# Revit family: Window-Awning-Marvin-Clad_Contemporary
name_source: partatom
category: Windows
revit_build: Autodesk Revit 2018 (Build: 20170223_1515(x64)
units: mm (PartAtom-declared; Revit-internal decimal feet)

## family parameters
Always vertical = Yes
Cut with Voids When Loaded = No
Host = Wall
OmniClass Number = 23.30.20.17.21.14
OmniClass Title = Casement Windows
Room Calculation Point = No
Shared = No

## types (240) — shared parameters
Bottom Rail Standard = Yes
Bottom Rail Tall = No
Cladding Material = Aluminum-Marvin-Bronze
Default Head Height = 8' - 0"
Frame = Aluminum Clad
Glass Type = IG Low E II with Argon
Glazing Material = Glass-Marvin-IG Low E II with Argon
Interior Material = Wood-Marvin-Pine
Jamb Extension Visibility = Yes
Label Visibility = No
Lite Cut HV Grid = Yes
Lite Cut Prairie 9 = No
Lite Cut Prairie 9 Constraint = No
Lites High = 2
Lites High Constraint = 2
Lites Wide = 4
Manufacturer = Marvin Windows and Doors
Muntins Exterior Material = Aluminum-Marvin-Bronze
Muntins Exterior Visibility = Yes
Muntins Interior Material = Wood-Marvin-Pine
Muntins Interior Visibility = Yes
Offset = 0' - 2 29/32"
Prairie Corner Height = 0' - 4"
Prairie Corner Width = 0' - 4"
URL = www.marvin.com
Wall Closure = By host
Window Type = Clad Contemporary Awning

## per-type parameters (varying)
| type | DLO Height | DLO Width | Daylight Area | Description | Design Pressure | Height | Lites Wide Constraint | Nominal Height | Nominal Width | Rough Height | Rough Width | VO Height | VO Width | Vent Area | Width |
| CCNTPRYAWN1614 | 0' - 7 5/16" | 0' - 10 3/16" | 0.52 SF | 1614 AWNG | DP50 | 1' - 1 1/8" | 2 | 1' - 2" | 1' - 4" | 1' - 1 5/8" | 1' - 5" | 0' - 8" | 0' - 6 13/32" | 0.36 SF | 1' - 4" |
| CCNTPRYAWN1616 | 0' - 9 5/16" | 0' - 10 3/16" | 0.66 SF | 1616 AWNG | DP50 | 1' - 3 1/8" | 2 | 1' - 4" | 1' - 4" | 1' - 3 5/8" | 1' - 5" | 0' - 10" | 0' - 6 13/32" | 0.45 SF | 1' - 4" |
| CCNTPRYAWN1618 | 0' - 11 5/16" | 0' - 10 3/16" | 0.8 SF | 1618 AWNG | DP50 | 1' - 5 1/8" | 2 | 1' - 6" | 1' - 4" | 1' - 5 5/8" | 1' - 5" | 1' - 0" | 0' - 6 13/32" | 0.53 SF | 1' - 4" |
| CCNTPRYAWN1620 | 1' - 1 5/16" | 0' - 10 3/16" | 0.94 SF | 1620 AWNG | DP50 | 1' - 7 1/8" | 2 | 1' - 8" | 1' - 4" | 1' - 7 5/8" | 1' - 5" | 1' - 2" | 0' - 6 13/32" | 0.62 SF | 1' - 4" |
| CCNTPRYAWN1624 | 1' - 5 5/16" | 0' - 10 3/16" | 1.22 SF | 1624 AWNG | DP50 | 1' - 11 1/8" | 2 | 2' - 0" | 1' - 4" | 1' - 11 5/8" | 1' - 5" | 1' - 6" | 0' - 6 13/32" | 0.8 SF | 1' - 4" |
| CCNTPRYAWN1628 | 1' - 9 5/16" | 0' - 10 3/16" | 1.51 SF | 1628 AWNG | DP50 | 2' - 3 1/8" | 2 | 2' - 4" | 1' - 4" | 2' - 3 5/8" | 1' - 5" | 1' - 10" | 0' - 6 13/32" | 0.98 SF | 1' - 4" |
| CCNTPRYAWN1632 | 2' - 1 5/16" | 0' - 10 3/16" | 1.79 SF | 1632 AWNG | DP50 | 2' - 7 1/8" | 2 | 2' - 8" | 1' - 4" | 2' - 7 5/8" | 1' - 5" | 2' - 2" | 0' - 6 13/32" | 1.16 SF | 1' - 4" |
| CCNTPRYAWN1636 | 2' - 5 5/16" | 0' - 10 3/16" | 2.07 SF | 1636 AWNG | DP50 | 2' - 11 1/8" | 2 | 3' - 0" | 1' - 4" | 2' - 11 5/8" | 1' - 5" | 2' - 6" | 0' - 6 13/32" | 1.34 SF | 1' - 4" |
| CCNTPRYAWN1640 | 2' - 9 5/16" | 0' - 10 3/16" | 2.36 SF | 1640 AWNG | DP50 | 3' - 3 1/8" | 2 | 3' - 4" | 1' - 4" | 3' - 3 5/8" | 1' - 5" | 2' - 10" | 0' - 6 13/32" | 1.51 SF | 1' - 4" |
| CCNTPRYAWN1644 | 3' - 1 5/16" | 0' - 10 3/16" | 2.64 SF | 1644 AWNG | DP50 | 3' - 7 1/8" | 2 | 3' - 8" | 1' - 4" | 3' - 7 5/8" | 1' - 5" | 3' - 2" | 0' - 6 13/32" | 1.69 SF | 1' - 4" |
| CCNTPRYAWN1648 | 3' - 5 5/16" | 0' - 10 3/16" | 2.92 SF | 1648 AWNG | DP50 | 3' - 11 1/8" | 2 | 4' - 0" | 1' - 4" | 3' - 11 5/8" | 1' - 5" | 3' - 6" | 0' - 6 13/32" | 1.87 SF | 1' - 4" |
| CCNTPRYAWN1654 | 3' - 11 5/16" | 0' - 10 3/16" | 3.35 SF | 1654 AWNG | DP50 | 4' - 5 1/8" | 2 | 4' - 6" | 1' - 4" | 4' - 5 5/8" | 1' - 5" | 4' - 0" | 0' - 6 13/32" | 2.14 SF | 1' - 4" |
| CCNTPRYAWN1656 | 4' - 1 5/16" | 0' - 10 3/16" | 3.49 SF | 1656 AWNG | DP50 | 4' - 7 1/8" | 2 | 4' - 8" | 1' - 4" | 4' - 7 5/8" | 1' - 5" | 4' - 2" | 0' - 6 13/32" | 2.22 SF | 1' - 4" |
| CCNTPRYAWN1660 | 4' - 5 5/16" | 0' - 10 3/16" | 3.77 SF | 1660 AWNG | DP50 | 4' - 11 1/8" | 2 | 5' - 0" | 1' - 4" | 4' - 11 5/8" | 1' - 5" | 4' - 6" | 0' - 6 13/32" | 2.4 SF | 1' - 4" |
| CCNTPRYAWN1664 | 4' - 9 5/16" | 0' - 10 3/16" | 4.05 SF | 1664 AWNG | DP50 | 5' - 3 1/8" | 2 | 5' - 4" | 1' - 4" | 5' - 3 5/8" | 1' - 5" | 4' - 10" | 0' - 6 13/32" | 2.58 SF | 1' - 4" |
| CCNTPRYAWN1672 | 5' - 5 5/16" | 0' - 10 3/16" | 4.62 SF | 1672 AWNG | DP50 | 5' - 11 1/8" | 2 | 6' - 0" | 1' - 4" | 5' - 11 5/8" | 1' - 5" | 5' - 6" | 0' - 6 13/32" | 2.94 SF | 1' - 4" |
| CCNTPRYAWN1814 | 0' - 7 5/16" | 1' - 0 3/16" | 0.62 SF | 1814 AWNG | DP50 | 1' - 1 1/8" | 4 | 1' - 2" | 1' - 6" | 1' - 1 5/8" | 1' - 7" | 0' - 8" | 0' - 8 13/32" | 0.47 SF | 1' - 6" |
| CCNTPRYAWN1816 | 0' - 9 5/16" | 1' - 0 3/16" | 0.79 SF | 1816 AWNG | DP50 | 1' - 3 1/8" | 4 | 1' - 4" | 1' - 6" | 1' - 3 5/8" | 1' - 7" | 0' - 10" | 0' - 8 13/32" | 0.58 SF | 1' - 6" |
| CCNTPRYAWN1818 | 0' - 11 5/16" | 1' - 0 3/16" | 0.96 SF | 1818 AWNG | DP50 | 1' - 5 1/8" | 4 | 1' - 6" | 1' - 6" | 1' - 5 5/8" | 1' - 7" | 1' - 0" | 0' - 8 13/32" | 0.7 SF | 1' - 6" |
| CCNTPRYAWN1820 | 1' - 1 5/16" | 1' - 0 3/16" | 1.13 SF | 1820 AWNG | DP50 | 1' - 7 1/8" | 4 | 1' - 8" | 1' - 6" | 1' - 7 5/8" | 1' - 7" | 1' - 2" | 0' - 8 13/32" | 0.82 SF | 1' - 6" |
| CCNTPRYAWN1824 | 1' - 5 5/16" | 1' - 0 3/16" | 1.47 SF | 1824 AWNG | DP50 | 1' - 11 1/8" | 4 | 2' - 0" | 1' - 6" | 1' - 11 5/8" | 1' - 7" | 1' - 6" | 0' - 8 13/32" | 1.05 SF | 1' - 6" |
| CCNTPRYAWN1828 | 1' - 9 5/16" | 1' - 0 3/16" | 1.8 SF | 1828 AWNG | DP50 | 2' - 3 1/8" | 4 | 2' - 4" | 1' - 6" | 2' - 3 5/8" | 1' - 7" | 1' - 10" | 0' - 8 13/32" | 1.28 SF | 1' - 6" |
| CCNTPRYAWN1832 | 2' - 1 5/16" | 1' - 0 3/16" | 2.14 SF | 1832 AWNG | DP50 | 2' - 7 1/8" | 4 | 2' - 8" | 1' - 6" | 2' - 7 5/8" | 1' - 7" | 2' - 2" | 0' - 8 13/32" | 1.52 SF | 1' - 6" |
| CCNTPRYAWN1836 | 2' - 5 5/16" | 1' - 0 3/16" | 2.48 SF | 1836 AWNG | DP50 | 2' - 11 1/8" | 4 | 3' - 0" | 1' - 6" | 2' - 11 5/8" | 1' - 7" | 2' - 6" | 0' - 8 13/32" | 1.75 SF | 1' - 6" |
| CCNTPRYAWN1840 | 2' - 9 5/16" | 1' - 0 3/16" | 2.82 SF | 1840 AWNG | DP50 | 3' - 3 1/8" | 4 | 3' - 4" | 1' - 6" | 3' - 3 5/8" | 1' - 7" | 2' - 10" | 0' - 8 13/32" | 1.99 SF | 1' - 6" |
| CCNTPRYAWN1844 | 3' - 1 5/16" | 1' - 0 3/16" | 3.16 SF | 1844 AWNG | DP50 | 3' - 7 1/8" | 4 | 3' - 8" | 1' - 6" | 3' - 7 5/8" | 1' - 7" | 3' - 2" | 0' - 8 13/32" | 2.22 SF | 1' - 6" |
| CCNTPRYAWN1848 | 3' - 5 5/16" | 1' - 0 3/16" | 3.5 SF | 1848 AWNG | DP50 | 3' - 11 1/8" | 4 | 4' - 0" | 1' - 6" | 3' - 11 5/8" | 1' - 7" | 3' - 6" | 0' - 8 13/32" | 2.45 SF | 1' - 6" |
| CCNTPRYAWN1854 | 3' - 11 5/16" | 1' - 0 3/16" | 4 SF | 1854 AWNG | DP50 | 4' - 5 1/8" | 4 | 4' - 6" | 1' - 6" | 4' - 5 5/8" | 1' - 7" | 4' - 0" | 0' - 8 13/32" | 2.8 SF | 1' - 6" |
| CCNTPRYAWN1856 | 4' - 1 5/16" | 1' - 0 3/16" | 4.17 SF | 1856 AWNG | DP50 | 4' - 7 1/8" | 4 | 4' - 8" | 1' - 6" | 4' - 7 5/8" | 1' - 7" | 4' - 2" | 0' - 8 13/32" | 2.92 SF | 1' - 6" |
| CCNTPRYAWN1860 | 4' - 5 5/16" | 1' - 0 3/16" | 4.51 SF | 1860 AWNG | DP50 | 4' - 11 1/8" | 4 | 5' - 0" | 1' - 6" | 4' - 11 5/8" | 1' - 7" | 4' - 6" | 0' - 8 13/32" | 3.15 SF | 1' - 6" |
| CCNTPRYAWN1864 | 4' - 9 5/16" | 1' - 0 3/16" | 4.85 SF | 1864 AWNG | DP50 | 5' - 3 1/8" | 4 | 5' - 4" | 1' - 6" | 5' - 3 5/8" | 1' - 7" | 4' - 10" | 0' - 8 13/32" | 3.39 SF | 1' - 6" |
| CCNTPRYAWN1872 | 5' - 5 5/16" | 1' - 0 3/16" | 5.53 SF | 1872 AWNG | DP50 | 5' - 11 1/8" | 4 | 6' - 0" | 1' - 6" | 5' - 11 5/8" | 1' - 7" | 5' - 6" | 0' - 8 13/32" | 3.85 SF | 1' - 6" |
| CCNTPRYAWN2014 | 0' - 7 5/16" | 1' - 2 3/16" | 0.72 SF | 2014 AWNG | DP50 | 1' - 1 1/8" | 4 | 1' - 2" | 1' - 8" | 1' - 1 5/8" | 1' - 9" | 0' - 8" | 1' - 0 29/32" | 0.72 SF | 1' - 8" |
| CCNTPRYAWN2016 | 0' - 9 5/16" | 1' - 2 3/16" | 0.92 SF | 2016 AWNG | DP50 | 1' - 3 1/8" | 4 | 1' - 4" | 1' - 8" | 1' - 3 5/8" | 1' - 9" | 0' - 10" | 1' - 0 29/32" | 0.9 SF | 1' - 8" |
| CCNTPRYAWN2018 | 0' - 11 5/16" | 1' - 2 3/16" | 1.11 SF | 2018 AWNG | DP50 | 1' - 5 1/8" | 4 | 1' - 6" | 1' - 8" | 1' - 5 5/8" | 1' - 9" | 1' - 0" | 1' - 0 29/32" | 1.08 SF | 1' - 8" |
| CCNTPRYAWN2020 | 1' - 1 5/16" | 1' - 2 3/16" | 1.31 SF | 2020 AWNG | DP50 | 1' - 7 1/8" | 4 | 1' - 8" | 1' - 8" | 1' - 7 5/8" | 1' - 9" | 1' - 2" | 1' - 0 29/32" | 1.25 SF | 1' - 8" |
| CCNTPRYAWN2024 | 1' - 5 5/16" | 1' - 2 3/16" | 1.71 SF | 2024 AWNG | DP50 | 1' - 11 1/8" | 4 | 2' - 0" | 1' - 8" | 1' - 11 5/8" | 1' - 9" | 1' - 6" | 1' - 0 29/32" | 1.61 SF | 1' - 8" |
| CCNTPRYAWN2028 | 1' - 9 5/16" | 1' - 2 3/16" | 2.1 SF | 2028 AWNG | DP50 | 2' - 3 1/8" | 4 | 2' - 4" | 1' - 8" | 2' - 3 5/8" | 1' - 9" | 1' - 10" | 1' - 0 29/32" | 1.97 SF | 1' - 8" |
| CCNTPRYAWN2032 | 2' - 1 5/16" | 1' - 2 3/16" | 2.49 SF | 2032 AWNG | DP50 | 2' - 7 1/8" | 4 | 2' - 8" | 1' - 8" | 2' - 7 5/8" | 1' - 9" | 2' - 2" | 1' - 0 29/32" | 2.33 SF | 1' - 8" |
| CCNTPRYAWN2036 | 2' - 5 5/16" | 1' - 2 3/16" | 2.89 SF | 2036 AWNG | DP50 | 2' - 11 1/8" | 4 | 3' - 0" | 1' - 8" | 2' - 11 5/8" | 1' - 9" | 2' - 6" | 1' - 0 29/32" | 2.69 SF | 1' - 8" |
| CCNTPRYAWN2040 | 2' - 9 5/16" | 1' - 2 3/16" | 3.28 SF | 2040 AWNG | DP50 | 3' - 3 1/8" | 4 | 3' - 4" | 1' - 8" | 3' - 3 5/8" | 1' - 9" | 2' - 10" | 1' - 0 29/32" | 3.04 SF | 1' - 8" |
| CCNTPRYAWN2044 | 3' - 1 5/16" | 1' - 2 3/16" | 3.68 SF | 2044 AWNG | DP50 | 3' - 7 1/8" | 4 | 3' - 8" | 1' - 8" | 3' - 7 5/8" | 1' - 9" | 3' - 2" | 1' - 0 29/32" | 3.4 SF | 1' - 8" |
| CCNTPRYAWN2048 | 3' - 5 5/16" | 1' - 2 3/16" | 4.07 SF | 2048 AWNG | DP50 | 3' - 11 1/8" | 4 | 4' - 0" | 1' - 8" | 3' - 11 5/8" | 1' - 9" | 3' - 6" | 1' - 0 29/32" | 3.76 SF | 1' - 8" |
| CCNTPRYAWN2054 | 3' - 11 5/16" | 1' - 2 3/16" | 4.66 SF | 2054 AWNG | DP50 | 4' - 5 1/8" | 4 | 4' - 6" | 1' - 8" | 4' - 5 5/8" | 1' - 9" | 4' - 0" | 1' - 0 29/32" | 4.3 SF | 1' - 8" |
| CCNTPRYAWN2056 | 4' - 1 5/16" | 1' - 2 3/16" | 4.86 SF | 2056 AWNG | DP50 | 4' - 7 1/8" | 4 | 4' - 8" | 1' - 8" | 4' - 7 5/8" | 1' - 9" | 4' - 2" | 1' - 0 29/32" | 4.48 SF | 1' - 8" |
| CCNTPRYAWN2060 | 4' - 5 5/16" | 1' - 2 3/16" | 5.25 SF | 2060 AWNG | DP50 | 4' - 11 1/8" | 4 | 5' - 0" | 1' - 8" | 4' - 11 5/8" | 1' - 9" | 4' - 6" | 1' - 0 29/32" | 4.84 SF | 1' - 8" |
| CCNTPRYAWN2064 | 4' - 9 5/16" | 1' - 2 3/16" | 5.65 SF | 2064 AWNG | DP50 | 5' - 3 1/8" | 4 | 5' - 4" | 1' - 8" | 5' - 3 5/8" | 1' - 9" | 4' - 10" | 1' - 0 29/32" | 5.19 SF | 1' - 8" |
| CCNTPRYAWN2072 | 5' - 5 5/16" | 1' - 2 3/16" | 6.43 SF | 2072 AWNG | DP50 | 5' - 11 1/8" | 4 | 6' - 0" | 1' - 8" | 5' - 11 5/8" | 1' - 9" | 5' - 6" | 1' - 0 29/32" | 5.91 SF | 1' - 8" |
| CCNTPRYAWN2414 | 0' - 7 5/16" | 1' - 6 3/16" | 0.92 SF | 2414 AWNG | DP50 | 1' - 1 1/8" | 4 | 1' - 2" | 2' - 0" | 1' - 1 5/8" | 2' - 1" | 0' - 8" | 1' - 4 29/32" | 0.94 SF | 2' - 0" |
| CCNTPRYAWN2416 | 0' - 9 5/16" | 1' - 6 3/16" | 1.18 SF | 2416 AWNG | DP50 | 1' - 3 1/8" | 4 | 1' - 4" | 2' - 0" | 1' - 3 5/8" | 2' - 1" | 0' - 10" | 1' - 4 29/32" | 1.17 SF | 2' - 0" |
| CCNTPRYAWN2418 | 0' - 11 5/16" | 1' - 6 3/16" | 1.43 SF | 2418 AWNG | DP50 | 1' - 5 1/8" | 4 | 1' - 6" | 2' - 0" | 1' - 5 5/8" | 2' - 1" | 1' - 0" | 1' - 4 29/32" | 1.41 SF | 2' - 0" |
| CCNTPRYAWN2420 | 1' - 1 5/16" | 1' - 6 3/16" | 1.68 SF | 2420 AWNG | DP50 | 1' - 7 1/8" | 4 | 1' - 8" | 2' - 0" | 1' - 7 5/8" | 2' - 1" | 1' - 2" | 1' - 4 29/32" | 1.64 SF | 2' - 0" |
| CCNTPRYAWN2424 | 1' - 5 5/16" | 1' - 6 3/16" | 2.19 SF | 2424 AWNG | DP50 | 1' - 11 1/8" | 4 | 2' - 0" | 2' - 0" | 1' - 11 5/8" | 2' - 1" | 1' - 6" | 1' - 4 29/32" | 2.11 SF | 2' - 0" |
| CCNTPRYAWN2428 | 1' - 9 5/16" | 1' - 6 3/16" | 2.69 SF | 2428 AWNG | DP50 | 2' - 3 1/8" | 4 | 2' - 4" | 2' - 0" | 2' - 3 5/8" | 2' - 1" | 1' - 10" | 1' - 4 29/32" | 2.58 SF | 2' - 0" |
| CCNTPRYAWN2432 | 2' - 1 5/16" | 1' - 6 3/16" | 3.2 SF | 2432 AWNG | DP50 | 2' - 7 1/8" | 4 | 2' - 8" | 2' - 0" | 2' - 7 5/8" | 2' - 1" | 2' - 2" | 1' - 4 29/32" | 3.05 SF | 2' - 0" |
| CCNTPRYAWN2436 | 2' - 5 5/16" | 1' - 6 3/16" | 3.7 SF | 2436 AWNG | DP50 | 2' - 11 1/8" | 4 | 3' - 0" | 2' - 0" | 2' - 11 5/8" | 2' - 1" | 2' - 6" | 1' - 4 29/32" | 3.52 SF | 2' - 0" |
| CCNTPRYAWN2440 | 2' - 9 5/16" | 1' - 6 3/16" | 4.21 SF | 2440 AWNG | DP50 | 3' - 3 1/8" | 4 | 3' - 4" | 2' - 0" | 3' - 3 5/8" | 2' - 1" | 2' - 10" | 1' - 4 29/32" | 3.99 SF | 2' - 0" |
| CCNTPRYAWN2444 | 3' - 1 5/16" | 1' - 6 3/16" | 4.71 SF | 2444 AWNG | DP50 | 3' - 7 1/8" | 4 | 3' - 8" | 2' - 0" | 3' - 7 5/8" | 2' - 1" | 3' - 2" | 1' - 4 29/32" | 4.46 SF | 2' - 0" |
| CCNTPRYAWN2448 | 3' - 5 5/16" | 1' - 6 3/16" | 5.22 SF | 2448 AWNG | DP50 | 3' - 11 1/8" | 4 | 4' - 0" | 2' - 0" | 3' - 11 5/8" | 2' - 1" | 3' - 6" | 1' - 4 29/32" | 4.93 SF | 2' - 0" |
| CCNTPRYAWN2454 | 3' - 11 5/16" | 1' - 6 3/16" | 5.98 SF | 2454 AWNG | DP50 | 4' - 5 1/8" | 4 | 4' - 6" | 2' - 0" | 4' - 5 5/8" | 2' - 1" | 4' - 0" | 1' - 4 29/32" | 5.63 SF | 2' - 0" |
| CCNTPRYAWN2456 | 4' - 1 5/16" | 1' - 6 3/16" | 6.23 SF | 2456 AWNG | DP50 | 4' - 7 1/8" | 4 | 4' - 8" | 2' - 0" | 4' - 7 5/8" | 2' - 1" | 4' - 2" | 1' - 4 29/32" | 5.87 SF | 2' - 0" |
| CCNTPRYAWN2460 | 4' - 5 5/16" | 1' - 6 3/16" | 6.73 SF | 2460 AWNG | DP50 | 4' - 11 1/8" | 4 | 5' - 0" | 2' - 0" | 4' - 11 5/8" | 2' - 1" | 4' - 6" | 1' - 4 29/32" | 6.34 SF | 2' - 0" |
| CCNTPRYAWN2464 | 4' - 9 5/16" | 1' - 6 3/16" | 7.24 SF | 2464 AWNG | DP50 | 5' - 3 1/8" | 4 | 5' - 4" | 2' - 0" | 5' - 3 5/8" | 2' - 1" | 4' - 10" | 1' - 4 29/32" | 6.8 SF | 2' - 0" |
| CCNTPRYAWN2472 | 5' - 5 5/16" | 1' - 6 3/16" | 8.25 SF | 2472 AWNG | DP50 | 5' - 11 1/8" | 4 | 6' - 0" | 2' - 0" | 5' - 11 5/8" | 2' - 1" | 5' - 6" | 1' - 4 29/32" | 7.74 SF | 2' - 0" |
| CCNTPRYAWN2614 | 0' - 7 5/16" | 1' - 8 3/16" | 1.03 SF | 2614 AWNG | DP50 | 1' - 1 1/8" | 4 | 1' - 2" | 2' - 2" | 1' - 1 5/8" | 2' - 3" | 0' - 8" | 1' - 6 29/32" | 1.05 SF | 2' - 2" |
| CCNTPRYAWN2616 | 0' - 9 5/16" | 1' - 8 3/16" | 1.31 SF | 2616 AWNG | DP50 | 1' - 3 1/8" | 4 | 1' - 4" | 2' - 2" | 1' - 3 5/8" | 2' - 3" | 0' - 10" | 1' - 6 29/32" | 1.31 SF | 2' - 2" |
| CCNTPRYAWN2618 | 0' - 11 5/16" | 1' - 8 3/16" | 1.59 SF | 2618 AWNG | DP50 | 1' - 5 1/8" | 4 | 1' - 6" | 2' - 2" | 1' - 5 5/8" | 2' - 3" | 1' - 0" | 1' - 6 29/32" | 1.58 SF | 2' - 2" |
| CCNTPRYAWN2620 | 1' - 1 5/16" | 1' - 8 3/16" | 1.87 SF | 2620 AWNG | DP50 | 1' - 7 1/8" | 4 | 1' - 8" | 2' - 2" | 1' - 7 5/8" | 2' - 3" | 1' - 2" | 1' - 6 29/32" | 1.84 SF | 2' - 2" |
| CCNTPRYAWN2624 | 1' - 5 5/16" | 1' - 8 3/16" | 2.43 SF | 2624 AWNG | DP50 | 1' - 11 1/8" | 4 | 2' - 0" | 2' - 2" | 1' - 11 5/8" | 2' - 3" | 1' - 6" | 1' - 6 29/32" | 2.36 SF | 2' - 2" |
| CCNTPRYAWN2628 | 1' - 9 5/16" | 1' - 8 3/16" | 2.99 SF | 2628 AWNG | DP50 | 2' - 3 1/8" | 4 | 2' - 4" | 2' - 2" | 2' - 3 5/8" | 2' - 3" | 1' - 10" | 1' - 6 29/32" | 2.89 SF | 2' - 2" |
| CCNTPRYAWN2632 | 2' - 1 5/16" | 1' - 8 3/16" | 3.55 SF | 2632 AWNG | DP50 | 2' - 7 1/8" | 4 | 2' - 8" | 2' - 2" | 2' - 7 5/8" | 2' - 3" | 2' - 2" | 1' - 6 29/32" | 3.41 SF | 2' - 2" |
| CCNTPRYAWN2636 | 2' - 5 5/16" | 1' - 8 3/16" | 4.11 SF | 2636 AWNG | DP50 | 2' - 11 1/8" | 4 | 3' - 0" | 2' - 2" | 2' - 11 5/8" | 2' - 3" | 2' - 6" | 1' - 6 29/32" | 3.94 SF | 2' - 2" |
| CCNTPRYAWN2640 | 2' - 9 5/16" | 1' - 8 3/16" | 4.67 SF | 2640 AWNG | DP50 | 3' - 3 1/8" | 4 | 3' - 4" | 2' - 2" | 3' - 3 5/8" | 2' - 3" | 2' - 10" | 1' - 6 29/32" | 4.46 SF | 2' - 2" |
| CCNTPRYAWN2644 | 3' - 1 5/16" | 1' - 8 3/16" | 5.23 SF | 2644 AWNG | DP50 | 3' - 7 1/8" | 4 | 3' - 8" | 2' - 2" | 3' - 7 5/8" | 2' - 3" | 3' - 2" | 1' - 6 29/32" | 4.99 SF | 2' - 2" |
| CCNTPRYAWN2648 | 3' - 5 5/16" | 1' - 8 3/16" | 5.79 SF | 2648 AWNG | DP50 | 3' - 11 1/8" | 4 | 4' - 0" | 2' - 2" | 3' - 11 5/8" | 2' - 3" | 3' - 6" | 1' - 6 29/32" | 5.51 SF | 2' - 2" |
| CCNTPRYAWN2654 | 3' - 11 5/16" | 1' - 8 3/16" | 6.63 SF | 2654 AWNG | DP50 | 4' - 5 1/8" | 4 | 4' - 6" | 2' - 2" | 4' - 5 5/8" | 2' - 3" | 4' - 0" | 1' - 6 29/32" | 6.3 SF | 2' - 2" |
| CCNTPRYAWN2656 | 4' - 1 5/16" | 1' - 8 3/16" | 6.91 SF | 2656 AWNG | DP50 | 4' - 7 1/8" | 4 | 4' - 8" | 2' - 2" | 4' - 7 5/8" | 2' - 3" | 4' - 2" | 1' - 6 29/32" | 6.56 SF | 2' - 2" |
| CCNTPRYAWN2660 | 4' - 5 5/16" | 1' - 8 3/16" | 7.47 SF | 2660 AWNG | DP50 | 4' - 11 1/8" | 4 | 5' - 0" | 2' - 2" | 4' - 11 5/8" | 2' - 3" | 4' - 6" | 1' - 6 29/32" | 7.09 SF | 2' - 2" |
| CCNTPRYAWN2664 | 4' - 9 5/16" | 1' - 8 3/16" | 8.03 SF | 2664 AWNG | DP50 | 5' - 3 1/8" | 4 | 5' - 4" | 2' - 2" | 5' - 3 5/8" | 2' - 3" | 4' - 10" | 1' - 6 29/32" | 7.61 SF | 2' - 2" |
| CCNTPRYAWN2672 | 5' - 5 5/16" | 1' - 8 3/16" | 9.16 SF | 2672 AWNG | DP50 | 5' - 11 1/8" | 4 | 6' - 0" | 2' - 2" | 5' - 11 5/8" | 2' - 3" | 5' - 6" | 1' - 6 29/32" | 8.66 SF | 2' - 2" |
| CCNTPRYAWN2814 | 0' - 7 5/16" | 1' - 10 3/16" | 1.13 SF | 2814 AWNG | DP50 | 1' - 1 1/8" | 4 | 1' - 2" | 2' - 4" | 1' - 1 5/8" | 2' - 5" | 0' - 8" | 1' - 8 29/32" | 1.16 SF | 2' - 4" |
| CCNTPRYAWN2816 | 0' - 9 5/16" | 1' - 10 3/16" | 1.43 SF | 2816 AWNG | DP50 | 1' - 3 1/8" | 4 | 1' - 4" | 2' - 4" | 1' - 3 5/8" | 2' - 5" | 0' - 10" | 1' - 8 29/32" | 1.45 SF | 2' - 4" |
| CCNTPRYAWN2818 | 0' - 11 5/16" | 1' - 10 3/16" | 1.74 SF | 2818 AWNG | DP50 | 1' - 5 1/8" | 4 | 1' - 6" | 2' - 4" | 1' - 5 5/8" | 2' - 5" | 1' - 0" | 1' - 8 29/32" | 1.74 SF | 2' - 4" |
| CCNTPRYAWN2820 | 1' - 1 5/16" | 1' - 10 3/16" | 2.05 SF | 2820 AWNG | DP50 | 1' - 7 1/8" | 4 | 1' - 8" | 2' - 4" | 1' - 7 5/8" | 2' - 5" | 1' - 2" | 1' - 8 29/32" | 2.03 SF | 2' - 4" |
| CCNTPRYAWN2824 | 1' - 5 5/16" | 1' - 10 3/16" | 2.67 SF | 2824 AWNG | DP50 | 1' - 11 1/8" | 4 | 2' - 0" | 2' - 4" | 1' - 11 5/8" | 2' - 5" | 1' - 6" | 1' - 8 29/32" | 2.61 SF | 2' - 4" |
| CCNTPRYAWN2828 | 1' - 9 5/16" | 1' - 10 3/16" | 3.28 SF | 2828 AWNG | DP50 | 2' - 3 1/8" | 4 | 2' - 4" | 2' - 4" | 2' - 3 5/8" | 2' - 5" | 1' - 10" | 1' - 8 29/32" | 3.19 SF | 2' - 4" |
| CCNTPRYAWN2832 | 2' - 1 5/16" | 1' - 10 3/16" | 3.9 SF | 2832 AWNG | DP50 | 2' - 7 1/8" | 4 | 2' - 8" | 2' - 4" | 2' - 7 5/8" | 2' - 5" | 2' - 2" | 1' - 8 29/32" | 3.77 SF | 2' - 4" |
| CCNTPRYAWN2836 | 2' - 5 5/16" | 1' - 10 3/16" | 4.52 SF | 2836 AWNG | DP50 | 2' - 11 1/8" | 4 | 3' - 0" | 2' - 4" | 2' - 11 5/8" | 2' - 5" | 2' - 6" | 1' - 8 29/32" | 4.35 SF | 2' - 4" |
| CCNTPRYAWN2840 | 2' - 9 5/16" | 1' - 10 3/16" | 5.13 SF | 2840 AWNG | DP50 | 3' - 3 1/8" | 4 | 3' - 4" | 2' - 4" | 3' - 3 5/8" | 2' - 5" | 2' - 10" | 1' - 8 29/32" | 4.93 SF | 2' - 4" |
| CCNTPRYAWN2844 | 3' - 1 5/16" | 1' - 10 3/16" | 5.75 SF | 2844 AWNG | DP50 | 3' - 7 1/8" | 4 | 3' - 8" | 2' - 4" | 3' - 7 5/8" | 2' - 5" | 3' - 2" | 1' - 8 29/32" | 5.51 SF | 2' - 4" |
| CCNTPRYAWN2848 | 3' - 5 5/16" | 1' - 10 3/16" | 6.37 SF | 2848 AWNG | DP50 | 3' - 11 1/8" | 4 | 4' - 0" | 2' - 4" | 3' - 11 5/8" | 2' - 5" | 3' - 6" | 1' - 8 29/32" | 6.09 SF | 2' - 4" |
| CCNTPRYAWN2854 | 3' - 11 5/16" | 1' - 10 3/16" | 7.29 SF | 2854 AWNG | DP50 | 4' - 5 1/8" | 4 | 4' - 6" | 2' - 4" | 4' - 5 5/8" | 2' - 5" | 4' - 0" | 1' - 8 29/32" | 6.97 SF | 2' - 4" |
| CCNTPRYAWN2856 | 4' - 1 5/16" | 1' - 10 3/16" | 7.6 SF | 2856 AWNG | DP50 | 4' - 7 1/8" | 4 | 4' - 8" | 2' - 4" | 4' - 7 5/8" | 2' - 5" | 4' - 2" | 1' - 8 29/32" | 7.26 SF | 2' - 4" |
| CCNTPRYAWN2860 | 4' - 5 5/16" | 1' - 10 3/16" | 8.21 SF | 2860 AWNG | DP50 | 4' - 11 1/8" | 4 | 5' - 0" | 2' - 4" | 4' - 11 5/8" | 2' - 5" | 4' - 6" | 1' - 8 29/32" | 7.84 SF | 2' - 4" |
| CCNTPRYAWN2864 | 4' - 9 5/16" | 1' - 10 3/16" | 8.83 SF | 2864 AWNG | DP50 | 5' - 3 1/8" | 4 | 5' - 4" | 2' - 4" | 5' - 3 5/8" | 2' - 5" | 4' - 10" | 1' - 8 29/32" | 8.42 SF | 2' - 4" |
| CCNTPRYAWN2872 | 5' - 5 5/16" | 1' - 10 3/16" | 10.06 SF | 2872 AWNG | DP50 | 5' - 11 1/8" | 4 | 6' - 0" | 2' - 4" | 5' - 11 5/8" | 2' - 5" | 5' - 6" | 1' - 8 29/32" | 9.58 SF | 2' - 4" |
| CCNTPRYAWN3014 | 0' - 7 5/16" | 2' - 0 3/16" | 1.23 SF | 3014 AWNG | DP50 | 1' - 1 1/8" | 4 | 1' - 2" | 2' - 6" | 1' - 1 5/8" | 2' - 7" | 0' - 8" | 1' - 10 29/32" | 1.27 SF | 2' - 6" |
| CCNTPRYAWN3016 | 0' - 9 5/16" | 2' - 0 3/16" | 1.56 SF | 3016 AWNG | DP50 | 1' - 3 1/8" | 4 | 1' - 4" | 2' - 6" | 1' - 3 5/8" | 2' - 7" | 0' - 10" | 1' - 10 29/32" | 1.59 SF | 2' - 6" |
| CCNTPRYAWN3018 | 0' - 11 5/16" | 2' - 0 3/16" | 1.9 SF | 3018 AWNG | DP50 | 1' - 5 1/8" | 4 | 1' - 6" | 2' - 6" | 1' - 5 5/8" | 2' - 7" | 1' - 0" | 1' - 10 29/32" | 1.91 SF | 2' - 6" |
| CCNTPRYAWN3020 | 1' - 1 5/16" | 2' - 0 3/16" | 2.24 SF | 3020 AWNG | DP50 | 1' - 7 1/8" | 4 | 1' - 8" | 2' - 6" | 1' - 7 5/8" | 2' - 7" | 1' - 2" | 1' - 10 29/32" | 2.23 SF | 2' - 6" |
| CCNTPRYAWN3024 | 1' - 5 5/16" | 2' - 0 3/16" | 2.91 SF | 3024 AWNG | DP50 | 1' - 11 1/8" | 4 | 2' - 0" | 2' - 6" | 1' - 11 5/8" | 2' - 7" | 1' - 6" | 1' - 10 29/32" | 2.86 SF | 2' - 6" |
| CCNTPRYAWN3028 | 1' - 9 5/16" | 2' - 0 3/16" | 3.58 SF | 3028 AWNG | DP50 | 2' - 3 1/8" | 4 | 2' - 4" | 2' - 6" | 2' - 3 5/8" | 2' - 7" | 1' - 10" | 1' - 10 29/32" | 3.5 SF | 2' - 6" |
| CCNTPRYAWN3032 | 2' - 1 5/16" | 2' - 0 3/16" | 4.25 SF | 3032 AWNG | DP50 | 2' - 7 1/8" | 4 | 2' - 8" | 2' - 6" | 2' - 7 5/8" | 2' - 7" | 2' - 2" | 1' - 10 29/32" | 4.13 SF | 2' - 6" |
| CCNTPRYAWN3036 | 2' - 5 5/16" | 2' - 0 3/16" | 4.92 SF | 3036 AWNG | DP50 | 2' - 11 1/8" | 4 | 3' - 0" | 2' - 6" | 2' - 11 5/8" | 2' - 7" | 2' - 6" | 1' - 10 29/32" | 4.77 SF | 2' - 6" |
| CCNTPRYAWN3040 | 2' - 9 5/16" | 2' - 0 3/16" | 5.6 SF | 3040 AWNG | DP50 | 3' - 3 1/8" | 4 | 3' - 4" | 2' - 6" | 3' - 3 5/8" | 2' - 7" | 2' - 10" | 1' - 10 29/32" | 5.41 SF | 2' - 6" |
| CCNTPRYAWN3044 | 3' - 1 5/16" | 2' - 0 3/16" | 6.27 SF | 3044 AWNG | DP50 | 3' - 7 1/8" | 4 | 3' - 8" | 2' - 6" | 3' - 7 5/8" | 2' - 7" | 3' - 2" | 1' - 10 29/32" | 6.04 SF | 2' - 6" |
| CCNTPRYAWN3048 | 3' - 5 5/16" | 2' - 0 3/16" | 6.94 SF | 3048 AWNG | DP50 | 3' - 11 1/8" | 4 | 4' - 0" | 2' - 6" | 3' - 11 5/8" | 2' - 7" | 3' - 6" | 1' - 10 29/32" | 6.68 SF | 2' - 6" |
| CCNTPRYAWN3054 | 3' - 11 5/16" | 2' - 0 3/16" | 7.95 SF | 3054 AWNG | DP50 | 4' - 5 1/8" | 4 | 4' - 6" | 2' - 6" | 4' - 5 5/8" | 2' - 7" | 4' - 0" | 1' - 10 29/32" | 7.63 SF | 2' - 6" |
| CCNTPRYAWN3056 | 4' - 1 5/16" | 2' - 0 3/16" | 8.28 SF | 3056 AWNG | DP50 | 4' - 7 1/8" | 4 | 4' - 8" | 2' - 6" | 4' - 7 5/8" | 2' - 7" | 4' - 2" | 1' - 10 29/32" | 7.95 SF | 2' - 6" |
| CCNTPRYAWN3060 | 4' - 5 5/16" | 2' - 0 3/16" | 8.95 SF | 3060 AWNG | DP50 | 4' - 11 1/8" | 4 | 5' - 0" | 2' - 6" | 4' - 11 5/8" | 2' - 7" | 4' - 6" | 1' - 10 29/32" | 8.59 SF | 2' - 6" |
| CCNTPRYAWN3064 | 4' - 9 5/16" | 2' - 0 3/16" | 9.63 SF | 3064 AWNG | DP50 | 5' - 3 1/8" | 4 | 5' - 4" | 2' - 6" | 5' - 3 5/8" | 2' - 7" | 4' - 10" | 1' - 10 29/32" | 9.22 SF | 2' - 6" |
| CCNTPRYAWN3072 | 5' - 5 5/16" | 2' - 0 3/16" | 10.97 SF | 3072 AWNG | DP50 | 5' - 11 1/8" | 4 | 6' - 0" | 2' - 6" | 5' - 11 5/8" | 2' - 7" | 5' - 6" | 1' - 10 29/32" | 10.49 SF | 2' - 6" |
| CCNTPRYAWN3214 | 0' - 7 5/16" | 2' - 2 3/16" | 1.33 SF | 3214 AWNG | DP50 | 1' - 1 1/8" | 4 | 1' - 2" | 2' - 8" | 1' - 1 5/8" | 2' - 9" | 0' - 8" | 2' - 0 29/32" | 1.38 SF | 2' - 8" |
| CCNTPRYAWN3216 | 0' - 9 5/16" | 2' - 2 3/16" | 1.69 SF | 3216 AWNG | DP50 | 1' - 3 1/8" | 4 | 1' - 4" | 2' - 8" | 1' - 3 5/8" | 2' - 9" | 0' - 10" | 2' - 0 29/32" | 1.73 SF | 2' - 8" |
| CCNTPRYAWN3218 | 0' - 11 5/16" | 2' - 2 3/16" | 2.06 SF | 3218 AWNG | DP50 | 1' - 5 1/8" | 4 | 1' - 6" | 2' - 8" | 1' - 5 5/8" | 2' - 9" | 1' - 0" | 2' - 0 29/32" | 2.08 SF | 2' - 8" |
| CCNTPRYAWN3220 | 1' - 1 5/16" | 2' - 2 3/16" | 2.42 SF | 3220 AWNG | DP50 | 1' - 7 1/8" | 4 | 1' - 8" | 2' - 8" | 1' - 7 5/8" | 2' - 9" | 1' - 2" | 2' - 0 29/32" | 2.42 SF | 2' - 8" |
| CCNTPRYAWN3224 | 1' - 5 5/16" | 2' - 2 3/16" | 3.15 SF | 3224 AWNG | DP50 | 1' - 11 1/8" | 4 | 2' - 0" | 2' - 8" | 1' - 11 5/8" | 2' - 9" | 1' - 6" | 2' - 0 29/32" | 3.11 SF | 2' - 8" |
| CCNTPRYAWN3228 | 1' - 9 5/16" | 2' - 2 3/16" | 3.88 SF | 3228 AWNG | DP50 | 2' - 3 1/8" | 4 | 2' - 4" | 2' - 8" | 2' - 3 5/8" | 2' - 9" | 1' - 10" | 2' - 0 29/32" | 3.8 SF | 2' - 8" |
| CCNTPRYAWN3232 | 2' - 1 5/16" | 2' - 2 3/16" | 4.6 SF | 3232 AWNG | DP50 | 2' - 7 1/8" | 4 | 2' - 8" | 2' - 8" | 2' - 7 5/8" | 2' - 9" | 2' - 2" | 2' - 0 29/32" | 4.5 SF | 2' - 8" |
| CCNTPRYAWN3236 | 2' - 5 5/16" | 2' - 2 3/16" | 5.33 SF | 3236 AWNG | DP50 | 2' - 11 1/8" | 4 | 3' - 0" | 2' - 8" | 2' - 11 5/8" | 2' - 9" | 2' - 6" | 2' - 0 29/32" | 5.19 SF | 2' - 8" |
| CCNTPRYAWN3240 | 2' - 9 5/16" | 2' - 2 3/16" | 6.06 SF | 3240 AWNG | DP50 | 3' - 3 1/8" | 4 | 3' - 4" | 2' - 8" | 3' - 3 5/8" | 2' - 9" | 2' - 10" | 2' - 0 29/32" | 5.88 SF | 2' - 8" |
| CCNTPRYAWN3244 | 3' - 1 5/16" | 2' - 2 3/16" | 6.79 SF | 3244 AWNG | DP50 | 3' - 7 1/8" | 4 | 3' - 8" | 2' - 8" | 3' - 7 5/8" | 2' - 9" | 3' - 2" | 2' - 0 29/32" | 6.57 SF | 2' - 8" |
| CCNTPRYAWN3248 | 3' - 5 5/16" | 2' - 2 3/16" | 7.51 SF | 3248 AWNG | DP50 | 3' - 11 1/8" | 4 | 4' - 0" | 2' - 8" | 3' - 11 5/8" | 2' - 9" | 3' - 6" | 2' - 0 29/32" | 7.26 SF | 2' - 8" |
| CCNTPRYAWN3254 | 3' - 11 5/16" | 2' - 2 3/16" | 8.6 SF | 3254 AWNG | DP50 | 4' - 5 1/8" | 4 | 4' - 6" | 2' - 8" | 4' - 5 5/8" | 2' - 9" | 4' - 0" | 2' - 0 29/32" | 8.3 SF | 2' - 8" |
| CCNTPRYAWN3256 | 4' - 1 5/16" | 2' - 2 3/16" | 8.97 SF | 3256 AWNG | DP50 | 4' - 7 1/8" | 4 | 4' - 8" | 2' - 8" | 4' - 7 5/8" | 2' - 9" | 4' - 2" | 2' - 0 29/32" | 8.64 SF | 2' - 8" |
| CCNTPRYAWN3260 | 4' - 5 5/16" | 2' - 2 3/16" | 9.7 SF | 3260 AWNG | DP50 | 4' - 11 1/8" | 4 | 5' - 0" | 2' - 8" | 4' - 11 5/8" | 2' - 9" | 4' - 6" | 2' - 0 29/32" | 9.34 SF | 2' - 8" |
| CCNTPRYAWN3264 | 4' - 9 5/16" | 2' - 2 3/16" | 10.42 SF | 3264 AWNG | DP50 | 5' - 3 1/8" | 4 | 5' - 4" | 2' - 8" | 5' - 3 5/8" | 2' - 9" | 4' - 10" | 2' - 0 29/32" | 10.03 SF | 2' - 8" |
| CCNTPRYAWN3272 | 5' - 5 5/16" | 2' - 2 3/16" | 11.88 SF | 3272 AWNG | DP50 | 5' - 11 1/8" | 4 | 6' - 0" | 2' - 8" | 5' - 11 5/8" | 2' - 9" | 5' - 6" | 2' - 0 29/32" | 11.41 SF | 2' - 8" |
| CCNTPRYAWN3614 | 0' - 7 5/16" | 2' - 6 3/16" | 1.53 SF | 3614 AWNG | DP50 | 1' - 1 1/8" | 4 | 1' - 2" | 3' - 0" | 1' - 1 5/8" | 3' - 1" | 0' - 8" | 2' - 4 29/32" | 1.61 SF | 3' - 0" |
| CCNTPRYAWN3616 | 0' - 9 5/16" | 2' - 6 3/16" | 1.95 SF | 3616 AWNG | DP50 | 1' - 3 1/8" | 4 | 1' - 4" | 3' - 0" | 1' - 3 5/8" | 3' - 1" | 0' - 10" | 2' - 4 29/32" | 2.01 SF | 3' - 0" |
| CCNTPRYAWN3618 | 0' - 11 5/16" | 2' - 6 3/16" | 2.37 SF | 3618 AWNG | DP50 | 1' - 5 1/8" | 4 | 1' - 6" | 3' - 0" | 1' - 5 5/8" | 3' - 1" | 1' - 0" | 2' - 4 29/32" | 2.41 SF | 3' - 0" |
| CCNTPRYAWN3620 | 1' - 1 5/16" | 2' - 6 3/16" | 2.79 SF | 3620 AWNG | DP50 | 1' - 7 1/8" | 4 | 1' - 8" | 3' - 0" | 1' - 7 5/8" | 3' - 1" | 1' - 2" | 2' - 4 29/32" | 2.81 SF | 3' - 0" |
| CCNTPRYAWN3624 | 1' - 5 5/16" | 2' - 6 3/16" | 3.63 SF | 3624 AWNG | DP50 | 1' - 11 1/8" | 4 | 2' - 0" | 3' - 0" | 1' - 11 5/8" | 3' - 1" | 1' - 6" | 2' - 4 29/32" | 3.61 SF | 3' - 0" |
| CCNTPRYAWN3628 | 1' - 9 5/16" | 2' - 6 3/16" | 4.47 SF | 3628 AWNG | DP50 | 2' - 3 1/8" | 4 | 2' - 4" | 3' - 0" | 2' - 3 5/8" | 3' - 1" | 1' - 10" | 2' - 4 29/32" | 4.42 SF | 3' - 0" |
| CCNTPRYAWN3632 | 2' - 1 5/16" | 2' - 6 3/16" | 5.31 SF | 3632 AWNG | DP50 | 2' - 7 1/8" | 4 | 2' - 8" | 3' - 0" | 2' - 7 5/8" | 3' - 1" | 2' - 2" | 2' - 4 29/32" | 5.22 SF | 3' - 0" |
| CCNTPRYAWN3636 | 2' - 5 5/16" | 2' - 6 3/16" | 6.14 SF | 3636 AWNG | DP50 | 2' - 11 1/8" | 4 | 3' - 0" | 3' - 0" | 2' - 11 5/8" | 3' - 1" | 2' - 6" | 2' - 4 29/32" | 6.02 SF | 3' - 0" |
| CCNTPRYAWN3640 | 2' - 9 5/16" | 2' - 6 3/16" | 6.98 SF | 3640 AWNG | DP50 | 3' - 3 1/8" | 4 | 3' - 4" | 3' - 0" | 3' - 3 5/8" | 3' - 1" | 2' - 10" | 2' - 4 29/32" | 6.82 SF | 3' - 0" |
| CCNTPRYAWN3644 | 3' - 1 5/16" | 2' - 6 3/16" | 7.82 SF | 3644 AWNG | DP50 | 3' - 7 1/8" | 4 | 3' - 8" | 3' - 0" | 3' - 7 5/8" | 3' - 1" | 3' - 2" | 2' - 4 29/32" | 7.63 SF | 3' - 0" |
| CCNTPRYAWN3648 | 3' - 5 5/16" | 2' - 6 3/16" | 8.66 SF | 3648 AWNG | DP50 | 3' - 11 1/8" | 4 | 4' - 0" | 3' - 0" | 3' - 11 5/8" | 3' - 1" | 3' - 6" | 2' - 4 29/32" | 8.43 SF | 3' - 0" |
| CCNTPRYAWN3654 | 3' - 11 5/16" | 2' - 6 3/16" | 9.92 SF | 3654 AWNG | DP50 | 4' - 5 1/8" | 4 | 4' - 6" | 3' - 0" | 4' - 5 5/8" | 3' - 1" | 4' - 0" | 2' - 4 29/32" | 9.63 SF | 3' - 0" |
| CCNTPRYAWN3656 | 4' - 1 5/16" | 2' - 6 3/16" | 10.34 SF | 3656 AWNG | DP50 | 4' - 7 1/8" | 4 | 4' - 8" | 3' - 0" | 4' - 7 5/8" | 3' - 1" | 4' - 2" | 2' - 4 29/32" | 10.03 SF | 3' - 0" |
| CCNTPRYAWN3660 | 4' - 5 5/16" | 2' - 6 3/16" | 11.18 SF | 3660 AWNG | DP50 | 4' - 11 1/8" | 4 | 5' - 0" | 3' - 0" | 4' - 11 5/8" | 3' - 1" | 4' - 6" | 2' - 4 29/32" | 10.84 SF | 3' - 0" |
| CCNTPRYAWN3664 | 4' - 9 5/16" | 2' - 6 3/16" | 12.01 SF | 3664 AWNG | DP50 | 5' - 3 1/8" | 4 | 5' - 4" | 3' - 0" | 5' - 3 5/8" | 3' - 1" | 4' - 10" | 2' - 4 29/32" | 11.64 SF | 3' - 0" |
| CCNTPRYAWN3672 | 5' - 5 5/16" | 2' - 6 3/16" | 13.69 SF | 3672 AWNG | DP50 | 5' - 11 1/8" | 4 | 6' - 0" | 3' - 0" | 5' - 11 5/8" | 3' - 1" | 5' - 6" | 2' - 4 29/32" | 13.24 SF | 3' - 0" |
| CCNTPRYAWN4014 | 0' - 7 5/16" | 2' - 10 3/16" | 1.74 SF | 4014 AWNG | DP50 | 1' - 1 1/8" | 4 | 1' - 2" | 3' - 4" | 1' - 1 5/8" | 3' - 5" | 0' - 8" | 2' - 8 29/32" | 1.83 SF | 3' - 4" |
| CCNTPRYAWN4016 | 0' - 9 5/16" | 2' - 10 3/16" | 2.21 SF | 4016 AWNG | DP50 | 1' - 3 1/8" | 4 | 1' - 4" | 3' - 4" | 1' - 3 5/8" | 3' - 5" | 0' - 10" | 2' - 8 29/32" | 2.29 SF | 3' - 4" |
| CCNTPRYAWN4018 | 0' - 11 5/16" | 2' - 10 3/16" | 2.69 SF | 4018 AWNG | DP50 | 1' - 5 1/8" | 4 | 1' - 6" | 3' - 4" | 1' - 5 5/8" | 3' - 5" | 1' - 0" | 2' - 8 29/32" | 2.74 SF | 3' - 4" |
| CCNTPRYAWN4020 | 1' - 1 5/16" | 2' - 10 3/16" | 3.16 SF | 4020 AWNG | DP50 | 1' - 7 1/8" | 4 | 1' - 8" | 3' - 4" | 1' - 7 5/8" | 3' - 5" | 1' - 2" | 2' - 8 29/32" | 3.2 SF | 3' - 4" |
| CCNTPRYAWN4024 | 1' - 5 5/16" | 2' - 10 3/16" | 4.11 SF | 4024 AWNG | DP50 | 1' - 11 1/8" | 4 | 2' - 0" | 3' - 4" | 1' - 11 5/8" | 3' - 5" | 1' - 6" | 2' - 8 29/32" | 4.11 SF | 3' - 4" |
| CCNTPRYAWN4028 | 1' - 9 5/16" | 2' - 10 3/16" | 5.06 SF | 4028 AWNG | DP50 | 2' - 3 1/8" | 4 | 2' - 4" | 3' - 4" | 2' - 3 5/8" | 3' - 5" | 1' - 10" | 2' - 8 29/32" | 5.03 SF | 3' - 4" |
| CCNTPRYAWN4032 | 2' - 1 5/16" | 2' - 10 3/16" | 6.01 SF | 4032 AWNG | DP50 | 2' - 7 1/8" | 4 | 2' - 8" | 3' - 4" | 2' - 7 5/8" | 3' - 5" | 2' - 2" | 2' - 8 29/32" | 5.94 SF | 3' - 4" |
| CCNTPRYAWN4036 | 2' - 5 5/16" | 2' - 10 3/16" | 6.96 SF | 4036 AWNG | DP50 | 2' - 11 1/8" | 4 | 3' - 0" | 3' - 4" | 2' - 11 5/8" | 3' - 5" | 2' - 6" | 2' - 8 29/32" | 6.85 SF | 3' - 4" |
| CCNTPRYAWN4040 | 2' - 9 5/16" | 2' - 10 3/16" | 7.91 SF | 4040 AWNG | DP50 | 3' - 3 1/8" | 4 | 3' - 4" | 3' - 4" | 3' - 3 5/8" | 3' - 5" | 2' - 10" | 2' - 8 29/32" | 7.77 SF | 3' - 4" |
| CCNTPRYAWN4044 | 3' - 1 5/16" | 2' - 10 3/16" | 8.86 SF | 4044 AWNG | DP50 | 3' - 7 1/8" | 4 | 3' - 8" | 3' - 4" | 3' - 7 5/8" | 3' - 5" | 3' - 2" | 2' - 8 29/32" | 8.68 SF | 3' - 4" |
| CCNTPRYAWN4048 | 3' - 5 5/16" | 2' - 10 3/16" | 9.81 SF | 4048 AWNG | DP50 | 3' - 11 1/8" | 4 | 4' - 0" | 3' - 4" | 3' - 11 5/8" | 3' - 5" | 3' - 6" | 2' - 8 29/32" | 9.6 SF | 3' - 4" |
| CCNTPRYAWN4054 | 3' - 11 5/16" | 2' - 10 3/16" | 11.23 SF | 4054 AWNG | DP50 | 4' - 5 1/8" | 4 | 4' - 6" | 3' - 4" | 4' - 5 5/8" | 3' - 5" | 4' - 0" | 2' - 8 29/32" | 10.97 SF | 3' - 4" |
| CCNTPRYAWN4056 | 4' - 1 5/16" | 2' - 10 3/16" | 11.71 SF | 4056 AWNG | DP50 | 4' - 7 1/8" | 4 | 4' - 8" | 3' - 4" | 4' - 7 5/8" | 3' - 5" | 4' - 2" | 2' - 8 29/32" | 11.42 SF | 3' - 4" |
| CCNTPRYAWN4060 | 4' - 5 5/16" | 2' - 10 3/16" | 12.66 SF | 4060 AWNG | DP50 | 4' - 11 1/8" | 4 | 5' - 0" | 3' - 4" | 4' - 11 5/8" | 3' - 5" | 4' - 6" | 2' - 8 29/32" | 12.34 SF | 3' - 4" |
| CCNTPRYAWN4064 | 4' - 9 5/16" | 2' - 10 3/16" | 13.61 SF | 4064 AWNG | DP50 | 5' - 3 1/8" | 4 | 5' - 4" | 3' - 4" | 5' - 3 5/8" | 3' - 5" | 4' - 10" | 2' - 8 29/32" | 13.25 SF | 3' - 4" |
| CCNTPRYAWN4072 | 5' - 5 5/16" | 2' - 10 3/16" | 15.51 SF | 4072 AWNG | DP50 | 5' - 11 1/8" | 4 | 6' - 0" | 3' - 4" | 5' - 11 5/8" | 3' - 5" | 5' - 6" | 2' - 8 29/32" | 15.08 SF | 3' - 4" |
| CCNTPRYAWN4814 | 0' - 7 5/16" | 3' - 6 3/16" | 2.14 SF | 4814 AWNG | DP50 | 1' - 1 1/8" | 4 | 1' - 2" | 4' - 0" | 1' - 1 5/8" | 4' - 1" | 0' - 8" | 3' - 4 29/32" | 2.28 SF | 4' - 0" |
| CCNTPRYAWN4816 | 0' - 9 5/16" | 3' - 6 3/16" | 2.73 SF | 4816 AWNG | DP50 | 1' - 3 1/8" | 4 | 1' - 4" | 4' - 0" | 1' - 3 5/8" | 4' - 1" | 0' - 10" | 3' - 4 29/32" | 2.84 SF | 4' - 0" |
| CCNTPRYAWN4818 | 0' - 11 5/16" | 3' - 6 3/16" | 3.31 SF | 4818 AWNG | DP50 | 1' - 5 1/8" | 4 | 1' - 6" | 4' - 0" | 1' - 5 5/8" | 4' - 1" | 1' - 0" | 3' - 4 29/32" | 3.41 SF | 4' - 0" |
| CCNTPRYAWN4820 | 1' - 1 5/16" | 3' - 6 3/16" | 3.9 SF | 4820 AWNG | DP50 | 1' - 7 1/8" | 4 | 1' - 8" | 4' - 0" | 1' - 7 5/8" | 4' - 1" | 1' - 2" | 3' - 4 29/32" | 3.98 SF | 4' - 0" |
| CCNTPRYAWN4824 | 1' - 5 5/16" | 3' - 6 3/16" | 5.07 SF | 4824 AWNG | DP50 | 1' - 11 1/8" | 4 | 2' - 0" | 4' - 0" | 1' - 11 5/8" | 4' - 1" | 1' - 6" | 3' - 4 29/32" | 5.11 SF | 4' - 0" |
| CCNTPRYAWN4828 | 1' - 9 5/16" | 3' - 6 3/16" | 6.24 SF | 4828 AWNG | DP50 | 2' - 3 1/8" | 4 | 2' - 4" | 4' - 0" | 2' - 3 5/8" | 4' - 1" | 1' - 10" | 3' - 4 29/32" | 6.25 SF | 4' - 0" |
| CCNTPRYAWN4832 | 2' - 1 5/16" | 3' - 6 3/16" | 7.42 SF | 4832 AWNG | DP50 | 2' - 7 1/8" | 4 | 2' - 8" | 4' - 0" | 2' - 7 5/8" | 4' - 1" | 2' - 2" | 3' - 4 29/32" | 7.39 SF | 4' - 0" |
| CCNTPRYAWN4836 | 2' - 5 5/16" | 3' - 6 3/16" | 8.59 SF | 4836 AWNG | DP50 | 2' - 11 1/8" | 4 | 3' - 0" | 4' - 0" | 2' - 11 5/8" | 4' - 1" | 2' - 6" | 3' - 4 29/32" | 8.52 SF | 4' - 0" |
| CCNTPRYAWN4840 | 2' - 9 5/16" | 3' - 6 3/16" | 9.76 SF | 4840 AWNG | DP50 | 3' - 3 1/8" | 4 | 3' - 4" | 4' - 0" | 3' - 3 5/8" | 4' - 1" | 2' - 10" | 3' - 4 29/32" | 9.66 SF | 4' - 0" |
| CCNTPRYAWN4844 | 3' - 1 5/16" | 3' - 6 3/16" | 10.93 SF | 4844 AWNG | DP50 | 3' - 7 1/8" | 4 | 3' - 8" | 4' - 0" | 3' - 7 5/8" | 4' - 1" | 3' - 2" | 3' - 4 29/32" | 10.79 SF | 4' - 0" |
| CCNTPRYAWN4848 | 3' - 5 5/16" | 3' - 6 3/16" | 12.1 SF | 4848 AWNG | DP50 | 3' - 11 1/8" | 4 | 4' - 0" | 4' - 0" | 3' - 11 5/8" | 4' - 1" | 3' - 6" | 3' - 4 29/32" | 11.93 SF | 4' - 0" |
| CCNTPRYAWN4854 | 3' - 11 5/16" | 3' - 6 3/16" | 13.86 SF | 4854 AWNG | DP50 | 4' - 5 1/8" | 4 | 4' - 6" | 4' - 0" | 4' - 5 5/8" | 4' - 1" | 4' - 0" | 3' - 4 29/32" | 13.63 SF | 4' - 0" |
| CCNTPRYAWN4856 | 4' - 1 5/16" | 3' - 6 3/16" | 14.45 SF | 4856 AWNG | DP50 | 4' - 7 1/8" | 4 | 4' - 8" | 4' - 0" | 4' - 7 5/8" | 4' - 1" | 4' - 2" | 3' - 4 29/32" | 14.2 SF | 4' - 0" |
| CCNTPRYAWN4860 | 4' - 5 5/16" | 3' - 6 3/16" | 15.62 SF | 4860 AWNG | DP50 | 4' - 11 1/8" | 4 | 5' - 0" | 4' - 0" | 4' - 11 5/8" | 4' - 1" | 4' - 6" | 3' - 4 29/32" | 15.34 SF | 4' - 0" |
| CCNTPRYAWN4864 | 4' - 9 5/16" | 3' - 6 3/16" | 16.79 SF | 4864 AWNG | DP50 | 5' - 3 1/8" | 4 | 5' - 4" | 4' - 0" | 5' - 3 5/8" | 4' - 1" | 4' - 10" | 3' - 4 29/32" | 16.47 SF | 4' - 0" |
| CCNTPRYAWN4872 | 5' - 5 5/16" | 3' - 6 3/16" | 19.13 SF | 4872 AWNG | DP50 | 5' - 11 1/8" | 4 | 6' - 0" | 4' - 0" | 5' - 11 5/8" | 4' - 1" | 5' - 6" | 3' - 4 29/32" | 18.74 SF | 4' - 0" |
| CCNTPRYAWN5614 | 0' - 7 5/16" | 4' - 2 3/16" | 2.55 SF | 5614 AWNG | DP50 | 1' - 1 1/8" | 4 | 1' - 2" | 4' - 8" | 1' - 1 5/8" | 4' - 9" | 0' - 8" | 4' - 0 29/32" | 2.72 SF | 4' - 8" |
| CCNTPRYAWN5616 | 0' - 9 5/16" | 4' - 2 3/16" | 3.25 SF | 5616 AWNG | DP50 | 1' - 3 1/8" | 4 | 1' - 4" | 4' - 8" | 1' - 3 5/8" | 4' - 9" | 0' - 10" | 4' - 0 29/32" | 3.4 SF | 4' - 8" |
| CCNTPRYAWN5618 | 0' - 11 5/16" | 4' - 2 3/16" | 3.94 SF | 5618 AWNG | DP50 | 1' - 5 1/8" | 4 | 1' - 6" | 4' - 8" | 1' - 5 5/8" | 4' - 9" | 1' - 0" | 4' - 0 29/32" | 4.08 SF | 4' - 8" |
| CCNTPRYAWN5620 | 1' - 1 5/16" | 4' - 2 3/16" | 4.64 SF | 5620 AWNG | DP50 | 1' - 7 1/8" | 4 | 1' - 8" | 4' - 8" | 1' - 7 5/8" | 4' - 9" | 1' - 2" | 4' - 0 29/32" | 4.76 SF | 4' - 8" |
| CCNTPRYAWN5624 | 1' - 5 5/16" | 4' - 2 3/16" | 6.03 SF | 5624 AWNG | DP50 | 1' - 11 1/8" | 4 | 2' - 0" | 4' - 8" | 1' - 11 5/8" | 4' - 9" | 1' - 6" | 4' - 0 29/32" | 6.12 SF | 4' - 8" |
| CCNTPRYAWN5628 | 1' - 9 5/16" | 4' - 2 3/16" | 7.43 SF | 5628 AWNG | DP50 | 2' - 3 1/8" | 4 | 2' - 4" | 4' - 8" | 2' - 3 5/8" | 4' - 9" | 1' - 10" | 4' - 0 29/32" | 7.47 SF | 4' - 8" |
| CCNTPRYAWN5632 | 2' - 1 5/16" | 4' - 2 3/16" | 8.82 SF | 5632 AWNG | DP50 | 2' - 7 1/8" | 4 | 2' - 8" | 4' - 8" | 2' - 7 5/8" | 4' - 9" | 2' - 2" | 4' - 0 29/32" | 8.83 SF | 4' - 8" |
| CCNTPRYAWN5636 | 2' - 5 5/16" | 4' - 2 3/16" | 10.22 SF | 5636 AWNG | DP50 | 2' - 11 1/8" | 4 | 3' - 0" | 4' - 8" | 2' - 11 5/8" | 4' - 9" | 2' - 6" | 4' - 0 29/32" | 10.19 SF | 4' - 8" |
| CCNTPRYAWN5640 | 2' - 9 5/16" | 4' - 2 3/16" | 11.61 SF | 5640 AWNG | DP50 | 3' - 3 1/8" | 4 | 3' - 4" | 4' - 8" | 3' - 3 5/8" | 4' - 9" | 2' - 10" | 4' - 0 29/32" | 11.55 SF | 4' - 8" |
| CCNTPRYAWN5644 | 3' - 1 5/16" | 4' - 2 3/16" | 13 SF | 5644 AWNG | DP50 | 3' - 7 1/8" | 4 | 3' - 8" | 4' - 8" | 3' - 7 5/8" | 4' - 9" | 3' - 2" | 4' - 0 29/32" | 12.91 SF | 4' - 8" |
| CCNTPRYAWN5648 | 3' - 5 5/16" | 4' - 2 3/16" | 14.4 SF | 5648 AWNG | DP50 | 3' - 11 1/8" | 4 | 4' - 0" | 4' - 8" | 3' - 11 5/8" | 4' - 9" | 3' - 6" | 4' - 0 29/32" | 14.26 SF | 4' - 8" |
| CCNTPRYAWN5654 | 3' - 11 5/16" | 4' - 2 3/16" | 16.49 SF | 5654 AWNG | DP50 | 4' - 5 1/8" | 4 | 4' - 6" | 4' - 8" | 4' - 5 5/8" | 4' - 9" | 4' - 0" | 4' - 0 29/32" | 16.3 SF | 4' - 8" |
| CCNTPRYAWN5656 | 4' - 1 5/16" | 4' - 2 3/16" | 17.19 SF | 5656 AWNG | DP50 | 4' - 7 1/8" | 4 | 4' - 8" | 4' - 8" | 4' - 7 5/8" | 4' - 9" | 4' - 2" | 4' - 0 29/32" | 16.98 SF | 4' - 8" |
| CCNTPRYAWN5660 | 4' - 5 5/16" | 4' - 2 3/16" | 18.58 SF | 5660 AWNG | DP50 | 4' - 11 1/8" | 4 | 5' - 0" | 4' - 8" | 4' - 11 5/8" | 4' - 9" | 4' - 6" | 4' - 0 29/32" | 18.34 SF | 4' - 8" |
| CCNTPRYAWN5664 | 4' - 9 5/16" | 4' - 2 3/16" | 19.97 SF | 5664 AWNG | DP40 | 5' - 3 1/8" | 4 | 5' - 4" | 4' - 8" | 5' - 3 5/8" | 4' - 9" | 4' - 10" | 4' - 0 29/32" | 19.7 SF | 4' - 8" |
| CCNTPRYAWN5672 | 5' - 5 5/16" | 4' - 2 3/16" | 22.76 SF | 5672 AWNG | DP40 | 5' - 11 1/8" | 4 | 6' - 0" | 4' - 8" | 5' - 11 5/8" | 4' - 9" | 5' - 6" | 4' - 0 29/32" | 22.41 SF | 4' - 8" |
| CCNTPRYAWN6014 | 0' - 7 5/16" | 4' - 6 3/16" | 2.75 SF | 6014 AWNG | DP50 | 1' - 1 1/8" | 4 | 1' - 2" | 5' - 0" | 1' - 1 5/8" | 5' - 1" | 0' - 8" | 4' - 4 29/32" | 2.94 SF | 5' - 0" |
| CCNTPRYAWN6016 | 0' - 9 5/16" | 4' - 6 3/16" | 3.5 SF | 6016 AWNG | DP50 | 1' - 3 1/8" | 4 | 1' - 4" | 5' - 0" | 1' - 3 5/8" | 5' - 1" | 0' - 10" | 4' - 4 29/32" | 3.68 SF | 5' - 0" |
| CCNTPRYAWN6018 | 0' - 11 5/16" | 4' - 6 3/16" | 4.26 SF | 6018 AWNG | DP50 | 1' - 5 1/8" | 4 | 1' - 6" | 5' - 0" | 1' - 5 5/8" | 5' - 1" | 1' - 0" | 4' - 4 29/32" | 4.41 SF | 5' - 0" |
| CCNTPRYAWN6020 | 1' - 1 5/16" | 4' - 6 3/16" | 5.01 SF | 6020 AWNG | DP50 | 1' - 7 1/8" | 4 | 1' - 8" | 5' - 0" | 1' - 7 5/8" | 5' - 1" | 1' - 2" | 4' - 4 29/32" | 5.15 SF | 5' - 0" |
| CCNTPRYAWN6024 | 1' - 5 5/16" | 4' - 6 3/16" | 6.51 SF | 6024 AWNG | DP50 | 1' - 11 1/8" | 4 | 2' - 0" | 5' - 0" | 1' - 11 5/8" | 5' - 1" | 1' - 6" | 4' - 4 29/32" | 6.62 SF | 5' - 0" |
| CCNTPRYAWN6028 | 1' - 9 5/16" | 4' - 6 3/16" | 8.02 SF | 6028 AWNG | DP50 | 2' - 3 1/8" | 4 | 2' - 4" | 5' - 0" | 2' - 3 5/8" | 5' - 1" | 1' - 10" | 4' - 4 29/32" | 8.08 SF | 5' - 0" |
| CCNTPRYAWN6032 | 2' - 1 5/16" | 4' - 6 3/16" | 9.53 SF | 6032 AWNG | DP50 | 2' - 7 1/8" | 4 | 2' - 8" | 5' - 0" | 2' - 7 5/8" | 5' - 1" | 2' - 2" | 4' - 4 29/32" | 9.55 SF | 5' - 0" |
| CCNTPRYAWN6036 | 2' - 5 5/16" | 4' - 6 3/16" | 11.03 SF | 6036 AWNG | DP50 | 2' - 11 1/8" | 4 | 3' - 0" | 5' - 0" | 2' - 11 5/8" | 5' - 1" | 2' - 6" | 4' - 4 29/32" | 11.02 SF | 5' - 0" |
| CCNTPRYAWN6040 | 2' - 9 5/16" | 4' - 6 3/16" | 12.54 SF | 6040 AWNG | DP50 | 3' - 3 1/8" | 4 | 3' - 4" | 5' - 0" | 3' - 3 5/8" | 5' - 1" | 2' - 10" | 4' - 4 29/32" | 12.49 SF | 5' - 0" |
| CCNTPRYAWN6044 | 3' - 1 5/16" | 4' - 6 3/16" | 14.04 SF | 6044 AWNG | DP50 | 3' - 7 1/8" | 4 | 3' - 8" | 5' - 0" | 3' - 7 5/8" | 5' - 1" | 3' - 2" | 4' - 4 29/32" | 13.96 SF | 5' - 0" |
| CCNTPRYAWN6048 | 3' - 5 5/16" | 4' - 6 3/16" | 15.55 SF | 6048 AWNG | DP50 | 3' - 11 1/8" | 4 | 4' - 0" | 5' - 0" | 3' - 11 5/8" | 5' - 1" | 3' - 6" | 4' - 4 29/32" | 15.43 SF | 5' - 0" |
| CCNTPRYAWN6054 | 3' - 11 5/16" | 4' - 6 3/16" | 17.8 SF | 6054 AWNG | DP40 | 4' - 5 1/8" | 4 | 4' - 6" | 5' - 0" | 4' - 5 5/8" | 5' - 1" | 4' - 0" | 4' - 4 29/32" | 17.63 SF | 5' - 0" |
| CCNTPRYAWN6056 | 4' - 1 5/16" | 4' - 6 3/16" | 18.56 SF | 6056 AWNG | DP40 | 4' - 7 1/8" | 4 | 4' - 8" | 5' - 0" | 4' - 7 5/8" | 5' - 1" | 4' - 2" | 4' - 4 29/32" | 18.37 SF | 5' - 0" |
| CCNTPRYAWN6060 | 4' - 5 5/16" | 4' - 6 3/16" | 20.06 SF | 6060 AWNG | DP40 | 4' - 11 1/8" | 4 | 5' - 0" | 5' - 0" | 4' - 11 5/8" | 5' - 1" | 4' - 6" | 4' - 4 29/32" | 19.84 SF | 5' - 0" |
| CCNTPRYAWN6064 | 4' - 9 5/16" | 4' - 6 3/16" | 21.57 SF | 6064 AWNG | DP40 | 5' - 3 1/8" | 4 | 5' - 4" | 5' - 0" | 5' - 3 5/8" | 5' - 1" | 4' - 10" | 4' - 4 29/32" | 21.31 SF | 5' - 0" |
| CCNTPRYAWN6072 | 5' - 5 5/16" | 4' - 6 3/16" | 24.58 SF | 6072 AWNG | DP40 | 5' - 11 1/8" | 4 | 6' - 0" | 5' - 0" | 5' - 11 5/8" | 5' - 1" | 5' - 6" | 4' - 4 29/32" | 24.25 SF | 5' - 0" |
| CCNTPRYAWN6414 | 0' - 7 5/16" | 4' - 10 3/16" | 2.95 SF | 6414 AWNG | DP50 | 1' - 1 1/8" | 4 | 1' - 2" | 5' - 4" | 1' - 1 5/8" | 5' - 5" | 0' - 8" | 4' - 8 29/32" | 3.17 SF | 5' - 4" |
| CCNTPRYAWN6416 | 0' - 9 5/16" | 4' - 10 3/16" | 3.76 SF | 6416 AWNG | DP50 | 1' - 3 1/8" | 4 | 1' - 4" | 5' - 4" | 1' - 3 5/8" | 5' - 5" | 0' - 10" | 4' - 8 29/32" | 3.96 SF | 5' - 4" |
| CCNTPRYAWN6418 | 0' - 11 5/16" | 4' - 10 3/16" | 4.57 SF | 6418 AWNG | DP50 | 1' - 5 1/8" | 4 | 1' - 6" | 5' - 4" | 1' - 5 5/8" | 5' - 5" | 1' - 0" | 4' - 8 29/32" | 4.75 SF | 5' - 4" |
| CCNTPRYAWN6420 | 1' - 1 5/16" | 4' - 10 3/16" | 5.38 SF | 6420 AWNG | DP50 | 1' - 7 1/8" | 4 | 1' - 8" | 5' - 4" | 1' - 7 5/8" | 5' - 5" | 1' - 2" | 4' - 8 29/32" | 5.54 SF | 5' - 4" |
| CCNTPRYAWN6424 | 1' - 5 5/16" | 4' - 10 3/16" | 7 SF | 6424 AWNG | DP50 | 1' - 11 1/8" | 4 | 2' - 0" | 5' - 4" | 1' - 11 5/8" | 5' - 5" | 1' - 6" | 4' - 8 29/32" | 7.12 SF | 5' - 4" |
| CCNTPRYAWN6428 | 1' - 9 5/16" | 4' - 10 3/16" | 8.61 SF | 6428 AWNG | DP50 | 2' - 3 1/8" | 4 | 2' - 4" | 5' - 4" | 2' - 3 5/8" | 5' - 5" | 1' - 10" | 4' - 8 29/32" | 8.7 SF | 5' - 4" |
| CCNTPRYAWN6432 | 2' - 1 5/16" | 4' - 10 3/16" | 10.23 SF | 6432 AWNG | DP50 | 2' - 7 1/8" | 4 | 2' - 8" | 5' - 4" | 2' - 7 5/8" | 5' - 5" | 2' - 2" | 4' - 8 29/32" | 10.28 SF | 5' - 4" |
| CCNTPRYAWN6436 | 2' - 5 5/16" | 4' - 10 3/16" | 11.84 SF | 6436 AWNG | DP50 | 2' - 11 1/8" | 4 | 3' - 0" | 5' - 4" | 2' - 11 5/8" | 5' - 5" | 2' - 6" | 4' - 8 29/32" | 11.86 SF | 5' - 4" |
| CCNTPRYAWN6440 | 2' - 9 5/16" | 4' - 10 3/16" | 13.46 SF | 6440 AWNG | DP50 | 3' - 3 1/8" | 4 | 3' - 4" | 5' - 4" | 3' - 3 5/8" | 5' - 5" | 2' - 10" | 4' - 8 29/32" | 13.44 SF | 5' - 4" |
| CCNTPRYAWN6444 | 3' - 1 5/16" | 4' - 10 3/16" | 15.08 SF | 6444 AWNG | DP50 | 3' - 7 1/8" | 4 | 3' - 8" | 5' - 4" | 3' - 7 5/8" | 5' - 5" | 3' - 2" | 4' - 8 29/32" | 15.02 SF | 5' - 4" |
| CCNTPRYAWN6448 | 3' - 5 5/16" | 4' - 10 3/16" | 16.69 SF | 6448 AWNG | DP50 | 3' - 11 1/8" | 4 | 4' - 0" | 5' - 4" | 3' - 11 5/8" | 5' - 5" | 3' - 6" | 4' - 8 29/32" | 16.6 SF | 5' - 4" |
| CCNTPRYAWN6454 | 3' - 11 5/16" | 4' - 10 3/16" | 19.12 SF | 6454 AWNG | DP40 | 4' - 5 1/8" | 4 | 4' - 6" | 5' - 4" | 4' - 5 5/8" | 5' - 5" | 4' - 0" | 4' - 8 29/32" | 18.97 SF | 5' - 4" |
| CCNTPRYAWN6456 | 4' - 1 5/16" | 4' - 10 3/16" | 19.93 SF | 6456 AWNG | DP40 | 4' - 7 1/8" | 4 | 4' - 8" | 5' - 4" | 4' - 7 5/8" | 5' - 5" | 4' - 2" | 4' - 8 29/32" | 19.76 SF | 5' - 4" |
| CCNTPRYAWN6460 | 4' - 5 5/16" | 4' - 10 3/16" | 21.54 SF | 6460 AWNG | DP40 | 4' - 11 1/8" | 4 | 5' - 0" | 5' - 4" | 4' - 11 5/8" | 5' - 5" | 4' - 6" | 4' - 8 29/32" | 21.34 SF | 5' - 4" |
| CCNTPRYAWN6464 | 4' - 9 5/16" | 4' - 10 3/16" | 23.16 SF | 6464 AWNG | DP40 | 5' - 3 1/8" | 4 | 5' - 4" | 5' - 4" | 5' - 3 5/8" | 5' - 5" | 4' - 10" | 4' - 8 29/32" | 22.92 SF | 5' - 4" |
| CCNTPRYAWN6472 | 5' - 5 5/16" | 4' - 10 3/16" | 26.39 SF | 6472 AWNG | DP40 | 5' - 11 1/8" | 4 | 6' - 0" | 5' - 4" | 5' - 11 5/8" | 5' - 5" | 5' - 6" | 4' - 8 29/32" | 26.08 SF | 5' - 4" |
| CCNTPRYAWN7214 | 0' - 7 5/16" | 5' - 6 3/16" | 3.36 SF | 7214 AWNG | DP50 | 1' - 1 1/8" | 4 | 1' - 2" | 6' - 0" | 1' - 1 5/8" | 6' - 1" | 0' - 8" | 5' - 4 29/32" | 3.61 SF | 6' - 0" |
| CCNTPRYAWN7216 | 0' - 9 5/16" | 5' - 6 3/16" | 4.28 SF | 7216 AWNG | DP50 | 1' - 3 1/8" | 4 | 1' - 4" | 6' - 0" | 1' - 3 5/8" | 6' - 1" | 0' - 10" | 5' - 4 29/32" | 4.51 SF | 6' - 0" |
| CCNTPRYAWN7218 | 0' - 11 5/16" | 5' - 6 3/16" | 5.2 SF | 7218 AWNG | DP50 | 1' - 5 1/8" | 4 | 1' - 6" | 6' - 0" | 1' - 5 5/8" | 6' - 1" | 1' - 0" | 5' - 4 29/32" | 5.41 SF | 6' - 0" |
| CCNTPRYAWN7220 | 1' - 1 5/16" | 5' - 6 3/16" | 6.12 SF | 7220 AWNG | DP50 | 1' - 7 1/8" | 4 | 1' - 8" | 6' - 0" | 1' - 7 5/8" | 6' - 1" | 1' - 2" | 5' - 4 29/32" | 6.31 SF | 6' - 0" |
| CCNTPRYAWN7224 | 1' - 5 5/16" | 5' - 6 3/16" | 7.96 SF | 7224 AWNG | DP50 | 1' - 11 1/8" | 4 | 2' - 0" | 6' - 0" | 1' - 11 5/8" | 6' - 1" | 1' - 6" | 5' - 4 29/32" | 8.12 SF | 6' - 0" |
| CCNTPRYAWN7228 | 1' - 9 5/16" | 5' - 6 3/16" | 9.8 SF | 7228 AWNG | DP50 | 2' - 3 1/8" | 4 | 2' - 4" | 6' - 0" | 2' - 3 5/8" | 6' - 1" | 1' - 10" | 5' - 4 29/32" | 9.92 SF | 6' - 0" |
| CCNTPRYAWN7232 | 2' - 1 5/16" | 5' - 6 3/16" | 11.63 SF | 7232 AWNG | DP50 | 2' - 7 1/8" | 4 | 2' - 8" | 6' - 0" | 2' - 7 5/8" | 6' - 1" | 2' - 2" | 5' - 4 29/32" | 11.72 SF | 6' - 0" |
| CCNTPRYAWN7236 | 2' - 5 5/16" | 5' - 6 3/16" | 13.47 SF | 7236 AWNG | DP50 | 2' - 11 1/8" | 4 | 3' - 0" | 6' - 0" | 2' - 11 5/8" | 6' - 1" | 2' - 6" | 5' - 4 29/32" | 13.52 SF | 6' - 0" |
| CCNTPRYAWN7240 | 2' - 9 5/16" | 5' - 6 3/16" | 15.31 SF | 7240 AWNG | DP50 | 3' - 3 1/8" | 4 | 3' - 4" | 6' - 0" | 3' - 3 5/8" | 6' - 1" | 2' - 10" | 5' - 4 29/32" | 15.33 SF | 6' - 0" |
| CCNTPRYAWN7244 | 3' - 1 5/16" | 5' - 6 3/16" | 17.15 SF | 7244 AWNG | DP50 | 3' - 7 1/8" | 4 | 3' - 8" | 6' - 0" | 3' - 7 5/8" | 6' - 1" | 3' - 2" | 5' - 4 29/32" | 17.13 SF | 6' - 0" |
| CCNTPRYAWN7248 | 3' - 5 5/16" | 5' - 6 3/16" | 18.99 SF | 7248 AWNG | DP50 | 3' - 11 1/8" | 4 | 4' - 0" | 6' - 0" | 3' - 11 5/8" | 6' - 1" | 3' - 6" | 5' - 4 29/32" | 18.93 SF | 6' - 0" |
| CCNTPRYAWN7254 | 3' - 11 5/16" | 5' - 6 3/16" | 21.75 SF | 7254 AWNG | DP40 | 4' - 5 1/8" | 4 | 4' - 6" | 6' - 0" | 4' - 5 5/8" | 6' - 1" | 4' - 0" | 5' - 4 29/32" | 21.64 SF | 6' - 0" |
| CCNTPRYAWN7256 | 4' - 1 5/16" | 5' - 6 3/16" | 22.67 SF | 7256 AWNG | DP40 | 4' - 7 1/8" | 4 | 4' - 8" | 6' - 0" | 4' - 7 5/8" | 6' - 1" | 4' - 2" | 5' - 4 29/32" | 22.54 SF | 6' - 0" |
| CCNTPRYAWN7260 | 4' - 5 5/16" | 5' - 6 3/16" | 24.5 SF | 7260 AWNG | DP40 | 4' - 11 1/8" | 4 | 5' - 0" | 6' - 0" | 4' - 11 5/8" | 6' - 1" | 4' - 6" | 5' - 4 29/32" | 24.34 SF | 6' - 0" |
| CCNTPRYAWN7264 | 4' - 9 5/16" | 5' - 6 3/16" | 26.34 SF | 7264 AWNG | DP40 | 5' - 3 1/8" | 4 | 5' - 4" | 6' - 0" | 5' - 3 5/8" | 6' - 1" | 4' - 10" | 5' - 4 29/32" | 26.14 SF | 6' - 0" |
| CCNTPRYAWN7272 | 5' - 5 5/16" | 5' - 6 3/16" | 30.02 SF | 7272 AWNG | DP40 | 5' - 11 1/8" | 4 | 6' - 0" | 6' - 0" | 5' - 11 5/8" | 6' - 1" | 5' - 6" | 5' - 4 29/32" | 29.75 SF | 6' - 0" |

note: column(s) folded — value = type name in every type: Model

## geometry (parser evidence)
native form markers: Blend x4, Sweep x10
no freeform markers — native parametric forms only
